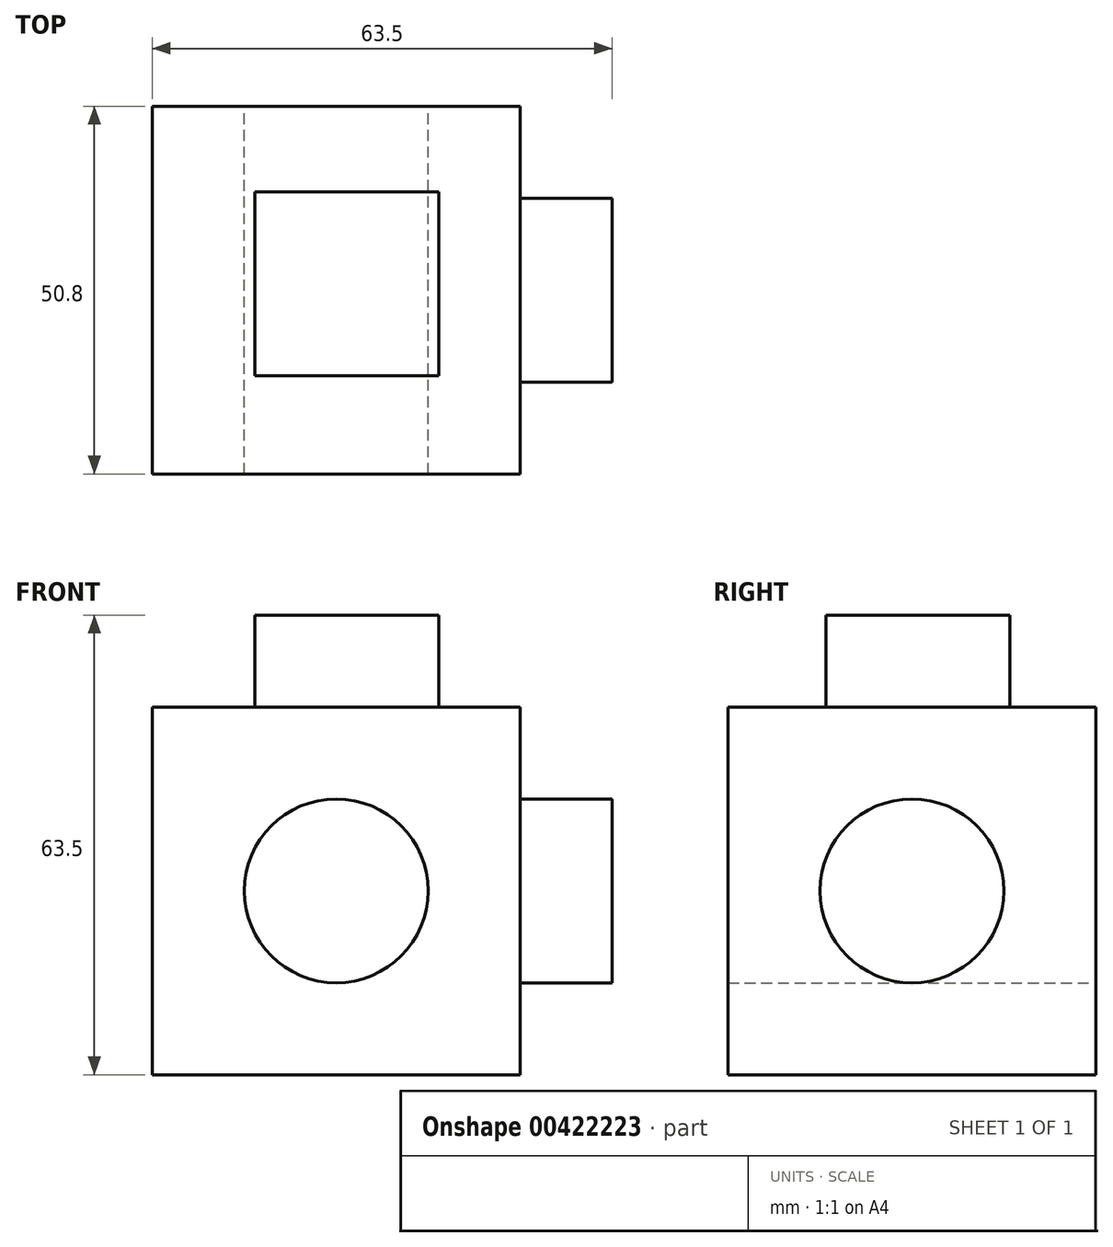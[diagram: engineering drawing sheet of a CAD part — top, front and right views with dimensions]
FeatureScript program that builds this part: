
annotation { "Feature Type Name" : "Feature", "Feature Type Description" : "" }
export const myFeature = defineFeature(function(context is Context, id is Id, definition is map)
    precondition{}
    {
        {
            var Q0;
            Q0=qCreatedBy(makeId("Front.planeOp"),FACE);
            var sketch = newSketch(context, id + "F0", { "sketchPlane" : qUnion([Q0])});
            skLineSegment(sketch, "E0.bottom", {"start": v(0, 0) * mm, "end": v(-50.8, 0) * mm});
            skLineSegment(sketch, "E0.top", {"start": v(0, 50.8) * mm, "end": v(-50.8, 50.8) * mm});
            skLineSegment(sketch, "E0.left", {"start": v(0, 0) * mm, "end": v(0, 50.8) * mm});
            skLineSegment(sketch, "E0.right", {"start": v(-50.8, 0) * mm, "end": v(-50.8, 50.8) * mm});
            skCircle(sketch, "E1", {"center": v(-25.4, 25.4) * mm, "radius": 12.7 * mm});
            skPoint(sketch, "E1.centerSnap0", {"position": v(-50.8, 25.4) * mm});
            skPoint(sketch, "E1.centerSnap1", {"position": v(-25.4, 0) * mm});
            skSolve(sketch);
        }
        {
            var Q0;
            Q0 = qSketchRegion(id + "F0", true);
            extrude(context, id + "F1", {"entities" : qUnion([Q0]), "depth" : 50.8 * mm, "offsetDistance" : 25.4 * mm});
        }
        {
            var Q0;
            Q0=makeQuery(id+"F1.opExtrude","SWEPT_FACE",FACE,{"disambiguationData":[OSD([sQuery(id+"F0.wireOp",EDGE,"E0.top")])]});
            var sketch = newSketch(context, id + "F2", { "sketchPlane" : qUnion([Q0])});
            skLineSegment(sketch, "E2.bottom", {"start": v(-36.67, -11.85) * mm, "end": v(-11.27, -11.85) * mm});
            skLineSegment(sketch, "E2.top", {"start": v(-36.67, -37.25) * mm, "end": v(-11.27, -37.25) * mm});
            skLineSegment(sketch, "E2.left", {"start": v(-36.67, -11.85) * mm, "end": v(-36.67, -37.25) * mm});
            skLineSegment(sketch, "E2.right", {"start": v(-11.27, -11.85) * mm, "end": v(-11.27, -37.25) * mm});
            skSolve(sketch);
        }
        {
            var Q0;
            Q0 = qSketchRegion(id + "F2", true);
            extrude(context, id + "F3", {"entities" : qUnion([Q0]), "operationType" : NewBodyOperationType.ADD, "depth" : 12.7 * mm, "offsetDistance" : 25.4 * mm});
        }
        {
            var Q0;
            Q0=makeQuery(id+"F1.opExtrude","SWEPT_FACE",FACE,{"disambiguationData":[OSD([sQuery(id+"F0.wireOp",EDGE,"E0.left")])]});
            var sketch = newSketch(context, id + "F4", { "sketchPlane" : qUnion([Q0])});
            skCircle(sketch, "E3", {"center": v(-25.4, 25.4) * mm, "radius": 12.7 * mm});
            skPoint(sketch, "E3.centerSnap0", {"position": v(-25.4, 50.8) * mm});
            skPoint(sketch, "E3.centerSnap1", {"position": v(-50.8, 25.4) * mm});
            skSolve(sketch);
        }
        {
            var Q0;
            Q0 = qSketchRegion(id + "F4", true);
            extrude(context, id + "F5", {"entities" : qUnion([Q0]), "operationType" : NewBodyOperationType.ADD, "depth" : 12.7 * mm, "offsetDistance" : 25.4 * mm});
        }
    });
